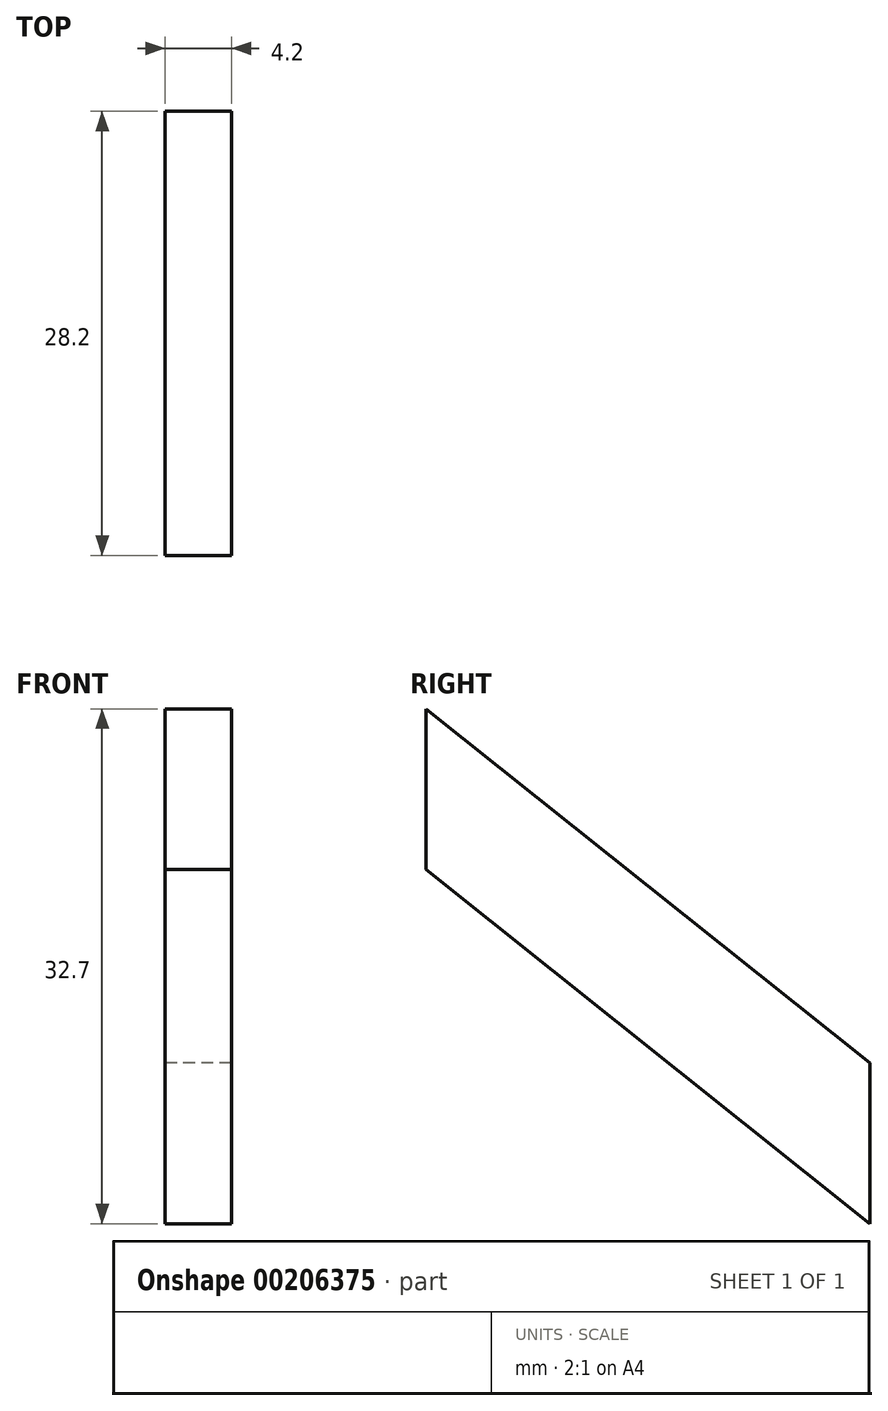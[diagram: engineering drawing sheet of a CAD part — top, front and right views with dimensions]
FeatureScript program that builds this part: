
annotation { "Feature Type Name" : "Feature", "Feature Type Description" : "" }
export const myFeature = defineFeature(function(context is Context, id is Id, definition is map)
    precondition{}
    {
        {
            var Q0;
            Q0=qCreatedBy(makeId("Right.planeOp"),FACE);
            var sketch = newSketch(context, id + "F0", { "sketchPlane" : qUnion([Q0])});
            skLineSegment(sketch, "E0", {"start": v(-28.2, 47.55) * mm, "end": v(-28.2, 37.35) * mm});
            skLineSegment(sketch, "E1", {"start": v(-28.2, 37.35) * mm, "end": v(0, 14.85) * mm});
            skLineSegment(sketch, "E2", {"start": v(0, 14.85) * mm, "end": v(0, 25.05) * mm});
            skLineSegment(sketch, "E3", {"start": v(0, 25.05) * mm, "end": v(-28.2, 47.55) * mm});
            skSolve(sketch);
        }
        {
            var Q0;
            Q0 = qSketchRegion(id + "F0", true);
            extrude(context, id + "F1", {"entities" : qUnion([Q0]), "depth" : 4.2 * mm});
        }
    });
